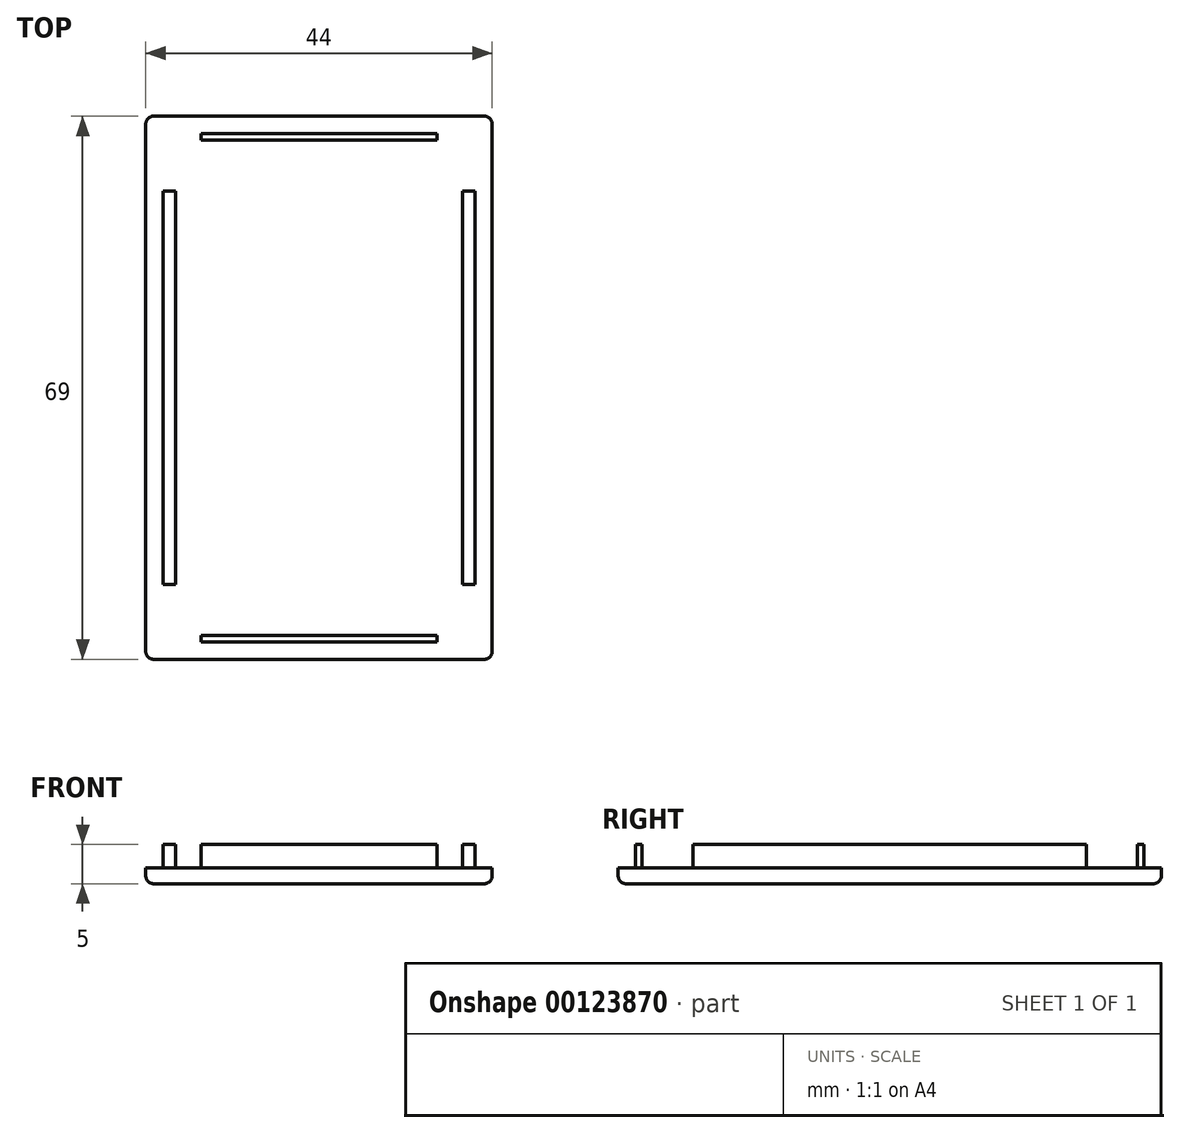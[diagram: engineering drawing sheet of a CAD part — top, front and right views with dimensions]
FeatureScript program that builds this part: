
annotation { "Feature Type Name" : "Feature", "Feature Type Description" : "" }
export const myFeature = defineFeature(function(context is Context, id is Id, definition is map)
    precondition{}
    {
        {
            var Q0;
            Q0=qCreatedBy(makeId("Top.planeOp"),FACE);
            var sketch = newSketch(context, id + "F0", { "sketchPlane" : qUnion([Q0])});
            skLineSegment(sketch, "E0.bottom", {"start": v(23, -34.5) * mm, "end": v(-19, -34.5) * mm});
            skLineSegment(sketch, "E0.top", {"start": v(23, 34.5) * mm, "end": v(-19, 34.5) * mm});
            skLineSegment(sketch, "E0.left", {"start": v(24, -33.5) * mm, "end": v(24, 33.5) * mm});
            skLineSegment(sketch, "E0.right", {"start": v(-20, -33.5) * mm, "end": v(-20, 33.5) * mm});
            skPoint(sketch, "E0.middle", {"position": v(0, 5.04) * mm});
            skLineSegment(sketch, "E1.bottom", {"start": v(-17.8, 25) * mm, "end": v(-16.2, 25) * mm});
            skLineSegment(sketch, "E1.top", {"start": v(-17.8, -25) * mm, "end": v(-16.2, -25) * mm});
            skLineSegment(sketch, "E1.left", {"start": v(-17.8, 25) * mm, "end": v(-17.8, -25) * mm});
            skLineSegment(sketch, "E1.right", {"start": v(-16.2, 25) * mm, "end": v(-16.2, -25) * mm});
            skLineSegment(sketch, "E2.bottom", {"start": v(21.8, 25) * mm, "end": v(20.2, 25) * mm});
            skLineSegment(sketch, "E2.top", {"start": v(21.8, -25) * mm, "end": v(20.2, -25) * mm});
            skLineSegment(sketch, "E2.left", {"start": v(21.8, 25) * mm, "end": v(21.8, -25) * mm});
            skLineSegment(sketch, "E2.right", {"start": v(20.2, 25) * mm, "end": v(20.2, -25) * mm});
            skLineSegment(sketch, "E3.bottom", {"start": v(-13, -31.46) * mm, "end": v(17, -31.46) * mm});
            skLineSegment(sketch, "E3.top", {"start": v(-13, -32.3) * mm, "end": v(17, -32.3) * mm});
            skLineSegment(sketch, "E3.left", {"start": v(-13, -31.46) * mm, "end": v(-13, -32.3) * mm});
            skLineSegment(sketch, "E3.right", {"start": v(17, -31.46) * mm, "end": v(17, -32.3) * mm});
            skLineSegment(sketch, "E4.MirrorCS", {"start": v(-13, 31.46) * mm, "end": v(-13, 32.3) * mm});
            skLineSegment(sketch, "E5.MirrorCS", {"start": v(17, 31.46) * mm, "end": v(17, 32.3) * mm});
            skLineSegment(sketch, "E6.MirrorCS", {"start": v(-13, 31.46) * mm, "end": v(17, 31.46) * mm});
            skLineSegment(sketch, "E7.MirrorCS", {"start": v(-13, 32.3) * mm, "end": v(17, 32.3) * mm});
            skPoint(sketch, "E8.visualSharp", {"position": v(-20, 34.5) * mm});
            skArc(sketch, "E8.filletArc", {"start": v(-19, 34.5) * mm, "mid": v(-19.7, 34.2) * mm, "end": v(-20, 33.5) * mm});
            skPoint(sketch, "E9.visualSharp", {"position": v(24, 34.5) * mm});
            skArc(sketch, "E9.filletArc", {"start": v(24, 33.5) * mm, "mid": v(23.7, 34.2) * mm, "end": v(23, 34.5) * mm});
            skPoint(sketch, "E10.visualSharp", {"position": v(-20, -34.5) * mm});
            skArc(sketch, "E10.filletArc", {"start": v(-20, -33.5) * mm, "mid": v(-19.7, -34.2) * mm, "end": v(-19, -34.5) * mm});
            skPoint(sketch, "E11.visualSharp", {"position": v(24, -34.5) * mm});
            skArc(sketch, "E11.filletArc", {"start": v(23, -34.5) * mm, "mid": v(23.7, -34.2) * mm, "end": v(24, -33.5) * mm});
            skSolve(sketch);
        }
        {
            var Q0;
            Q0=makeQuery(id+"F0.imprint","IMPRINT",FACE,{"disambiguationData":[TD([[makeQuery(id+"F0.imprint","IMPRINT",EDGE,{"derivedFrom":sQuery(id+"F0.wireOp",EDGE,"E0.bottom")}),-1.0]])]});
            extrude(context, id + "F1", {"entities" : qUnion([Q0]), "depth" : 2 * mm});
        }
        {
            var Q0;
            Q0=makeQuery(id+"F0.imprint","IMPRINT",FACE,{"disambiguationData":[TD([[makeQuery(id+"F0.imprint","IMPRINT",EDGE,{"derivedFrom":sQuery(id+"F0.wireOp",EDGE,"E1.bottom")}),-1.0]])]});
            var Q1;
            Q1=makeQuery(id+"F0.imprint","IMPRINT",FACE,{"disambiguationData":[TD([[makeQuery(id+"F0.imprint","IMPRINT",EDGE,{"derivedFrom":sQuery(id+"F0.wireOp",EDGE,"E4.MirrorCS")}),-1.0]])]});
            var Q2;
            Q2=makeQuery(id+"F0.imprint","IMPRINT",FACE,{"disambiguationData":[TD([[makeQuery(id+"F0.imprint","IMPRINT",EDGE,{"derivedFrom":sQuery(id+"F0.wireOp",EDGE,"E2.bottom")}),1.0]])]});
            var Q3;
            Q3=makeQuery(id+"F0.imprint","IMPRINT",FACE,{"disambiguationData":[TD([[makeQuery(id+"F0.imprint","IMPRINT",EDGE,{"derivedFrom":sQuery(id+"F0.wireOp",EDGE,"E3.bottom")}),-1.0]])]});
            extrude(context, id + "F2", {"entities" : qUnion([Q0, Q1, Q2, Q3]), "operationType" : NewBodyOperationType.ADD, "depth" : 5 * mm});
        }
        {
            var Q0;
            {var subQ0=sQuery(id+"F0.wireOp",EDGE,"E7.MirrorCS");var subQ1=sQuery(id+"F0.wireOp",EDGE,"E6.MirrorCS");var subQ2=sQuery(id+"F0.wireOp",EDGE,"E5.MirrorCS");var subQ3=sQuery(id+"F0.wireOp",EDGE,"E4.MirrorCS");var subQ4=sQuery(id+"F0.wireOp",EDGE,"E3.right");var subQ5=sQuery(id+"F0.wireOp",EDGE,"E3.left");var subQ6=sQuery(id+"F0.wireOp",EDGE,"E3.top");var subQ7=sQuery(id+"F0.wireOp",EDGE,"E3.bottom");var subQ8=sQuery(id+"F0.wireOp",EDGE,"E2.right");var subQ9=sQuery(id+"F0.wireOp",EDGE,"E2.left");var subQ10=sQuery(id+"F0.wireOp",EDGE,"E2.top");var subQ11=sQuery(id+"F0.wireOp",EDGE,"E2.bottom");var subQ12=sQuery(id+"F0.wireOp",EDGE,"E1.right");var subQ13=sQuery(id+"F0.wireOp",EDGE,"E1.left");var subQ14=sQuery(id+"F0.wireOp",EDGE,"E1.top");var subQ15=sQuery(id+"F0.wireOp",EDGE,"E1.bottom");Q0=makeQuery(id+"F2.boolean.opBoolean","MERGE",FACE,{"derivedFrom":[makeQuery(id+"F1.opExtrude","CAP_FACE",FACE,{"disambiguationData":[OSD([sQuery(id+"F0.wireOp",EDGE,"E0.bottom"),sQuery(id+"F0.wireOp",EDGE,"E0.top"),sQuery(id+"F0.wireOp",EDGE,"E0.left"),sQuery(id+"F0.wireOp",EDGE,"E0.right"),subQ15,subQ14,subQ13,subQ12,subQ11,subQ10,subQ9,subQ8,subQ7,subQ6,subQ5,subQ4,subQ3,subQ2,subQ1,subQ0,sQuery(id+"F0.wireOp",EDGE,"E8.filletArc"),sQuery(id+"F0.wireOp",EDGE,"E9.filletArc"),sQuery(id+"F0.wireOp",EDGE,"E10.filletArc"),sQuery(id+"F0.wireOp",EDGE,"E11.filletArc")])],"isStart":true}),makeQuery(id+"F2.opExtrude","CAP_FACE",FACE,{"disambiguationData":[OSD([subQ15,subQ14,subQ13,subQ12])],"isStart":true}),makeQuery(id+"F2.opExtrude","CAP_FACE",FACE,{"disambiguationData":[OSD([subQ11,subQ10,subQ9,subQ8])],"isStart":true}),makeQuery(id+"F2.opExtrude","CAP_FACE",FACE,{"disambiguationData":[OSD([subQ7,subQ6,subQ5,subQ4])],"isStart":true}),makeQuery(id+"F2.opExtrude","CAP_FACE",FACE,{"disambiguationData":[OSD([subQ3,subQ2,subQ1,subQ0])],"isStart":true})]});}
            fillet(context, id + "F3", {"entities" : qUnion([Q0]), "radius" : 1 * mm, "tangentPropagation" : true, "allowEdgeOverflow" : false});
        }
    });
